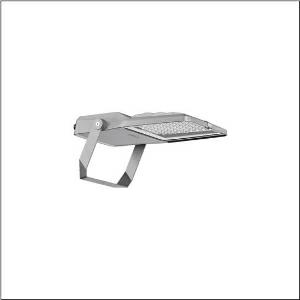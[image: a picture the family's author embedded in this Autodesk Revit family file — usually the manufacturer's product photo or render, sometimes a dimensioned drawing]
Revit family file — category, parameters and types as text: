
# Revit family: floodlight_fl_21_mini___pl64_5xa7776c4e1a_25dc
name_source: partatom
category: Lighting Fixtures
units: mm (PartAtom-declared; Revit-internal decimal feet)

## family parameters
Cut with Voids When Loaded = No
Host = Face
Light Source = No
Part Type = Normal
Room Calculation Point = No
Round Connector Dimension = Use Diameter
Shared = No

## types (1)
- --- (1 x LED, 12260 lm, 89 W, 4000K)
    Apparent Load = 89 VA
    CIE Flux Codes = 28 80 98 100 100
    Color Rendering = 70
    Color Temperature = 4000K
    Default Elevation = 1800 mm
    Description = Floodlight FL 21 mini, floodlight, primary light control with lens, of PMMA, primary optical cover: protective disc, of toughened safety glass, transparent, light distribution: PL64, light emission: direct distribution, installation type: surface-mounted, LED, High Power LED, rated luminous flux: 12.260lm, luminous efficacy: 138lm/W, light colour: 740, colour temperature: 4000K, control gear: D4iSmart Interface (Zhaga), control: overheat protection, constant luminous flux control, time-dependent luminous flux control, flexible luminous flux parameterisation, pre-setting: logarithmic dimming characteristic, with terminal, 6-pole, mains connection: 220..240V, AC, 50/60Hz, start of lifetime: 89W, end of service life: 94W, reduction: 43W, mounting bracket, of diecast aluminium, powder-coated, SITECO metallic grey (DB 702S), corrosivity category C5 mid according to DIN EN ISO 12944, suitable for swimming pools, chlorine-resistant, sealing non-destructively replaceable, mounting bracket, of steel, galvanised, powder-coated, SITECO metallic grey (DB 702S), Smart Interface below and above, protection rating (complete): IP66, insulation class (complete): insulation class II (safety insulation), certification: CE, ENEC, VDE, protection symbol: D, impact resistance: IK08, permissible operating ambient temperature: -40..+40°C, permissible operating ambient temperature for outdoor applications: -40..+50°C, standard: DIN EN 12944, LABS conformity tested according to VDMA 24364:2018-05, packaging unit: 1 piece

Light Distribution: PL64
    Height = 70 mm
    Lamp = 1 x LED
    Lamp Light Flux = 12260 lm
    Lamp Power = 89 W
    Lamp count = 1
    Length = 485 mm
    Luminous efficacy = 138 lm/W
    Manufacturer = Siteco
    ModVariant = No
    Model = 5XA7776C4E1A
    Number of Poles = 1
    OnlyDefault = Yes
    Power Factor = 1
    Product Name = Floodlight FL 21 mini | PL64
    Product group = floodlight | pylon annexe
    ProductGroupID = 6201
    Protection Class = Protection class II
    Protection Degree = IP 66
    RLX_Detail_Level = 1
    RLX_Emergency_Light_Flux = 0 lm
    RLX_Emergency_Type = 0
    RLX_Emergency_Type_DB = No
    RlxData = <blob elided: 96041 chars, md5=c9d9681a>
    Socket = socket
    Standby Power = 0 W
    System Light Flux = 12260 lm
    System Power = 89 W
    Type Comments = factory setting: luminous flux: 100 % | dim-lin: 254 | 456 mA
    Type Image = l_1006845.jpg
    URL = http://relux.com
    VarID = @adj_100011
    Voltage = 0 V
    Weight = 0.00 kg
    Width = 337 mm

## geometry (parser evidence)
native form markers: Blend x4, Sweep x10
no freeform markers — native parametric forms only
